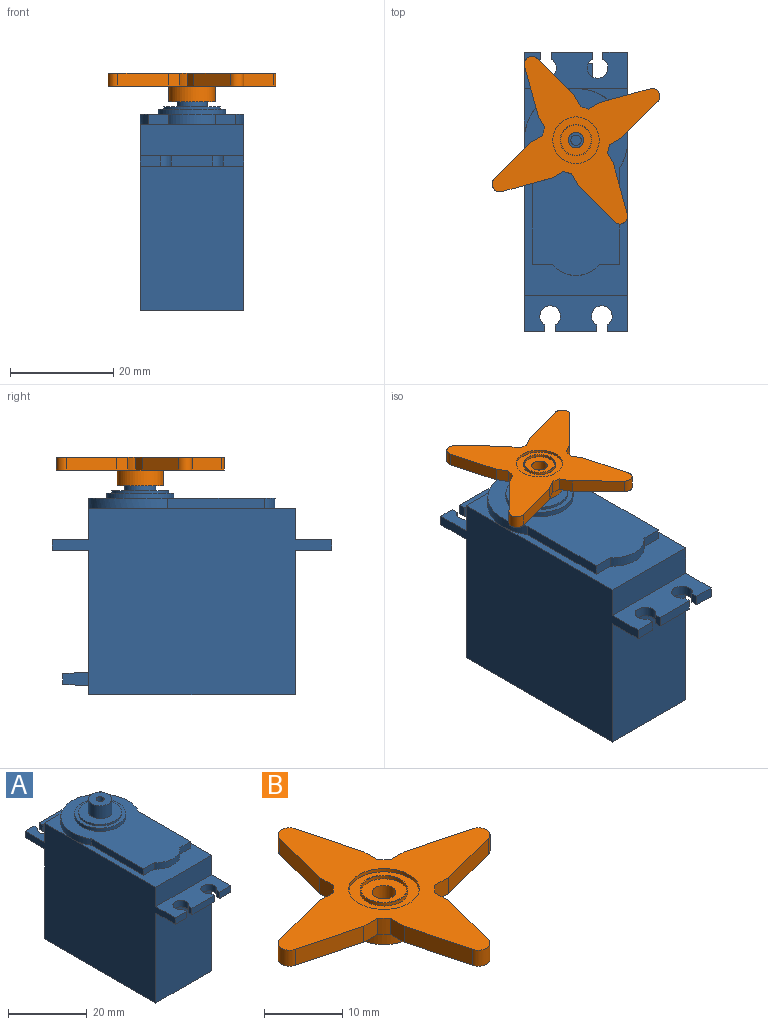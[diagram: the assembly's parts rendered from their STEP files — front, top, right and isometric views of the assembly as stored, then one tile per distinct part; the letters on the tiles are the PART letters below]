
ASSEMBLY  parts=2 mates=1
PART A: 52 faces, bbox 20x54x43.5 mm
  f0: plane 8x2mm, normal (0,1,0), area 16mm2, adj f2,f13,f33,f37
  f1: plane 3.18x2mm, normal (0,1,0), area 6.4mm2, adj f2,f13,f19,f34
  f2: plane 20x7mm, normal (0,0,-1), area 110.5mm2, adj f0,f1,f11,f12,f18,f19,f33,f34
  f3: plane 8x2mm, normal (0,-1,0), area 16mm2, adj f5,f6,f28,f30
  f4: plane 4x2mm, normal (0,-1,0), area 8mm2, adj f5,f6,f18,f29
  f5: plane 20x7mm, normal (0,0,1), area 110.5mm2, adj f3,f4,f16,f17,f18,f19,f27,f28
  f6: plane 20x7mm, normal (0,0,-1), area 110.5mm2, adj f3,f4,f9,f17,f18,f19,f27,f28
  f7: plane 10x10mm, normal (0,0,1), area 21.5mm2, adj f14,f19,f23
  f8: plane 10x10mm, normal (0,0,1), area 21.5mm2, adj f14,f18,f23
  f9: plane 28x20mm, normal (0,-1,0), area 560mm2, adj f6,f10,f18,f19
  f10: plane 40x20mm, normal (0,0,-1), area 800mm2, adj f9,f11,f18,f19
  f11: plane 28x20mm, normal (0,1,0), area 543.8mm2, adj f2,f10,f18,f19,f39,f40,f41,f42
  f12: plane 4.82x2mm, normal (0,1,0), area 9.6mm2, adj f2,f13,f18,f36
  f13: plane 20x7mm, normal (0,0,1), area 110.5mm2, adj f0,f1,f12,f14,f18,f19,f33,f34
  f14: plane 20x6mm, normal (0,1,0), area 120mm2, adj f7,f8,f13,f18,f19
  f15: plane 30x20mm, normal (0,0,1), area 167.4mm2, adj f16,f18,f19,f20,f21,f22,f23,f24
  f16: plane 20x6mm, normal (0,-1,0), area 120mm2, adj f5,f15,f18,f19
  f17: plane 4x2mm, normal (0,-1,0), area 8mm2, adj f5,f6,f19,f32
  f18: plane 54x36mm, normal (1,0,0), area 1468mm2, adj f2,f4,f5,f6,f8,f9,f10,f11
  f19: plane 54x36mm, normal (-1,0,0), area 1468mm2, adj f1,f2,f5,f6,f7,f9,f10,f11
  f20: cylinder r=5.96mm len=9.18mm, axis (0,0,-1), area 21mm2, adj f15,f21,f25,f26
  f21: plane 3.91x2mm, normal (0,-1,0), area 7.8mm2, adj f15,f20,f22,f26
  f22: plane 18.73x2mm, normal (1,0,0), area 37.5mm2, adj f15,f21,f23,f26
  f23: cylinder r=10mm len=20mm, axis (0,0,-1), area 85mm2, adj f7,f8,f15,f22,f24,f26
  f24: plane 18.73x2mm, normal (-1,0,0), area 37.5mm2, adj f15,f23,f25,f26
  f25: plane 3.91x2mm, normal (0,-1,0), area 7.8mm2, adj f15,f20,f24,f26
  f26: plane 36.16x20mm, normal (0,0,1), area 456.8mm2, adj f20,f21,f22,f23,f24,f25,f44
  f27: cylinder r=2mm len=4mm, axis (0,0,1), area 20.9mm2, adj f5,f6,f28,f29
  f28: plane 2x1.27mm, normal (1,0,0), area 2.5mm2, adj f3,f5,f6,f27
  f29: plane 2x1.27mm, normal (-1,0,0), area 2.5mm2, adj f4,f5,f6,f27
  f30: plane 2x1.27mm, normal (-1,0,0), area 2.5mm2, adj f3,f5,f6,f31
  f31: cylinder r=2mm len=4mm, axis (0,0,1), area 20.9mm2, adj f5,f6,f30,f32
  f32: plane 2x1.27mm, normal (1,0,0), area 2.5mm2, adj f5,f6,f17,f31
  f33: plane 2x1.27mm, normal (-1,0,0), area 2.5mm2, adj f0,f2,f13,f35
  f34: plane 2x1.27mm, normal (1,0,0), area 2.5mm2, adj f1,f2,f13,f35
  f35: cylinder r=2mm len=4mm, axis (0,0,1), area 20.9mm2, adj f2,f13,f33,f34
  f36: plane 2x1.27mm, normal (-1,0,0), area 2.5mm2, adj f2,f12,f13,f38
  f37: plane 2x1.27mm, normal (1,0,0), area 2.5mm2, adj f0,f2,f13,f38
  f38: cylinder r=2mm len=4mm, axis (0,0,1), area 20.9mm2, adj f2,f13,f36,f37
  f39: plane 6.22x5mm, normal (0,0.05,1), area 29.8mm2, adj f11,f40,f42,f43
  f40: plane 5x2.61mm, normal (1,0.05,0), area 11.7mm2, adj f11,f39,f41,f43
  f41: plane 6.22x5mm, normal (0,0.05,-1), area 29.8mm2, adj f11,f40,f42,f43
  f42: plane 5x2.61mm, normal (-1,0.05,0), area 11.7mm2, adj f11,f39,f41,f43
  f43: plane 5.69x2.08mm, normal (0,1,0), area 11.9mm2, adj f39,f40,f41,f42
  f44: cylinder r=6.5mm len=13mm, axis (0,0,-1), area 40.8mm2, adj f26,f45
  f45: plane 13x13mm, normal (0,0,1), area 37.7mm2, adj f44,f46
  f46: cylinder r=5.5mm len=11mm, axis (0,0,-1), area 17.3mm2, adj f45,f47
  f47: plane 11x11mm, normal (0,0,1), area 66.8mm2, adj f46,f48
  f48: cylinder r=3mm len=6mm, axis (0,0,-1), area 75.4mm2, adj f47,f49
  f49: plane 6x6mm, normal (0,0,1), area 25.1mm2, adj f48,f50
  f50: cylinder r=1mm len=5mm, axis (0,0,1), area 31.4mm2, adj f49,f51
  f51: plane 2x2mm, normal (0,0,1), area 3.1mm2, adj f50
PART B: 37 faces, bbox 37x37x5.5 mm
  f0: cylinder r=1.5mm len=3mm, axis (0,0,1), area 18.8mm2, adj f30,f32
  f1: cylinder r=1.5mm len=2.9mm, axis (0,0,-1), area 9.9mm2, adj f2,f24,f25,f26
  f2: plane 9.76x2.55mm, normal (-0.25,-0.97,0), area 25.2mm2, adj f1,f3,f25,f26
  f3: plane 2.5x2.5mm, normal (0,-1,0), area 6.3mm2, adj f2,f4,f25,f26
  f4: cylinder r=6.5mm len=2.5mm, axis (0,0,-1), area 4mm2, adj f3,f5,f25,f26
  f5: plane 2.5x2.5mm, normal (-1,0,0), area 6.2mm2, adj f4,f6,f25,f26
  f6: plane 9.76x2.55mm, normal (-0.97,-0.25,0), area 25.2mm2, adj f5,f7,f25,f26
  f7: cylinder r=1.5mm len=2.9mm, axis (0,0,-1), area 9.9mm2, adj f6,f8,f25,f26
  f8: plane 9.76x2.55mm, normal (0.97,-0.25,0), area 25.2mm2, adj f7,f9,f25,f26
  f9: plane 2.5x2.5mm, normal (1,0,0), area 6.2mm2, adj f8,f10,f25,f26
  f10: cylinder r=6.5mm len=2.5mm, axis (0,0,-1), area 4mm2, adj f9,f11,f25,f26
  f11: plane 2.5x2.5mm, normal (0,-1,0), area 6.3mm2, adj f10,f12,f25,f26
  f12: plane 9.76x2.55mm, normal (0.25,-0.97,0), area 25.2mm2, adj f11,f13,f25,f26
  f13: cylinder r=1.5mm len=2.9mm, axis (0,0,-1), area 9.9mm2, adj f12,f14,f25,f26
  f14: plane 9.76x2.55mm, normal (0.25,0.97,0), area 25.2mm2, adj f13,f15,f25,f26
  f15: plane 2.5x2.5mm, normal (0,1,0), area 6.3mm2, adj f14,f16,f25,f26
  f16: cylinder r=6.5mm len=2.5mm, axis (0,0,-1), area 4mm2, adj f15,f17,f25,f26
  f17: plane 2.5x2.5mm, normal (1,0,0), area 6.3mm2, adj f16,f18,f25,f26
  f18: plane 9.76x2.55mm, normal (0.97,0.25,0), area 25.2mm2, adj f17,f19,f25,f26
  f19: cylinder r=1.5mm len=2.9mm, axis (0,0,-1), area 9.9mm2, adj f18,f20,f25,f26
  f20: plane 9.76x2.55mm, normal (-0.97,0.25,0), area 25.2mm2, adj f19,f21,f25,f26
  f21: plane 2.5x2.5mm, normal (-1,0,0), area 6.3mm2, adj f20,f22,f25,f26
  f22: cylinder r=6.5mm len=2.5mm, axis (0,0,-1), area 4mm2, adj f21,f23,f25,f26
  f23: plane 2.5x2.5mm, normal (0,1,0), area 6.3mm2, adj f22,f24,f25,f26
  f24: plane 9.76x2.55mm, normal (-0.25,0.97,0), area 25.2mm2, adj f1,f23,f25,f26
  f25: plane 37x37mm, normal (0,0,1), area 341.4mm2, adj f1,f2,f3,f4,f5,f6,f7,f8
  f26: plane 37x37mm, normal (0,0,-1), area 341.4mm2, adj f1,f2,f3,f4,f5,f6,f7,f8
  f27: cylinder r=4.5mm len=9mm, axis (0,0,1), area 84.8mm2, adj f26,f28
  f28: plane 9x9mm, normal (0,0,-1), area 35.3mm2, adj f27,f29
  f29: cylinder r=3mm len=6mm, axis (0,0,-1), area 56.5mm2, adj f28,f30
  f30: plane 6x6mm, normal (0,0,-1), area 21.2mm2, adj f0,f29
  f31: cylinder r=2.95mm len=5.9mm, axis (0,0,1), area 9.3mm2, adj f32,f36
  f32: plane 5.9x5.9mm, normal (0,0,1), area 20.3mm2, adj f0,f31
  f33: cylinder r=3.05mm len=6.1mm, axis (0,0,1), area 9.6mm2, adj f35,f36
  f34: cylinder r=4.5mm len=9mm, axis (0,0,1), area 14.1mm2, adj f25,f35
  f35: plane 9x9mm, normal (0,0,1), area 34.4mm2, adj f33,f34
  f36: plane 6.1x6.1mm, normal (0,0,1), area 1.9mm2, adj f31,f33
PLACE A t=(-16.97,-9.58,11.61)mm
PLACE B rot(axis=(0,0,1),30deg) t=(15.73,-6.23,10.94)mm
MATE revolute B.f0 <-> A.f23  axis (0,0,1) through (-6.97,53.01,40.74)mm
